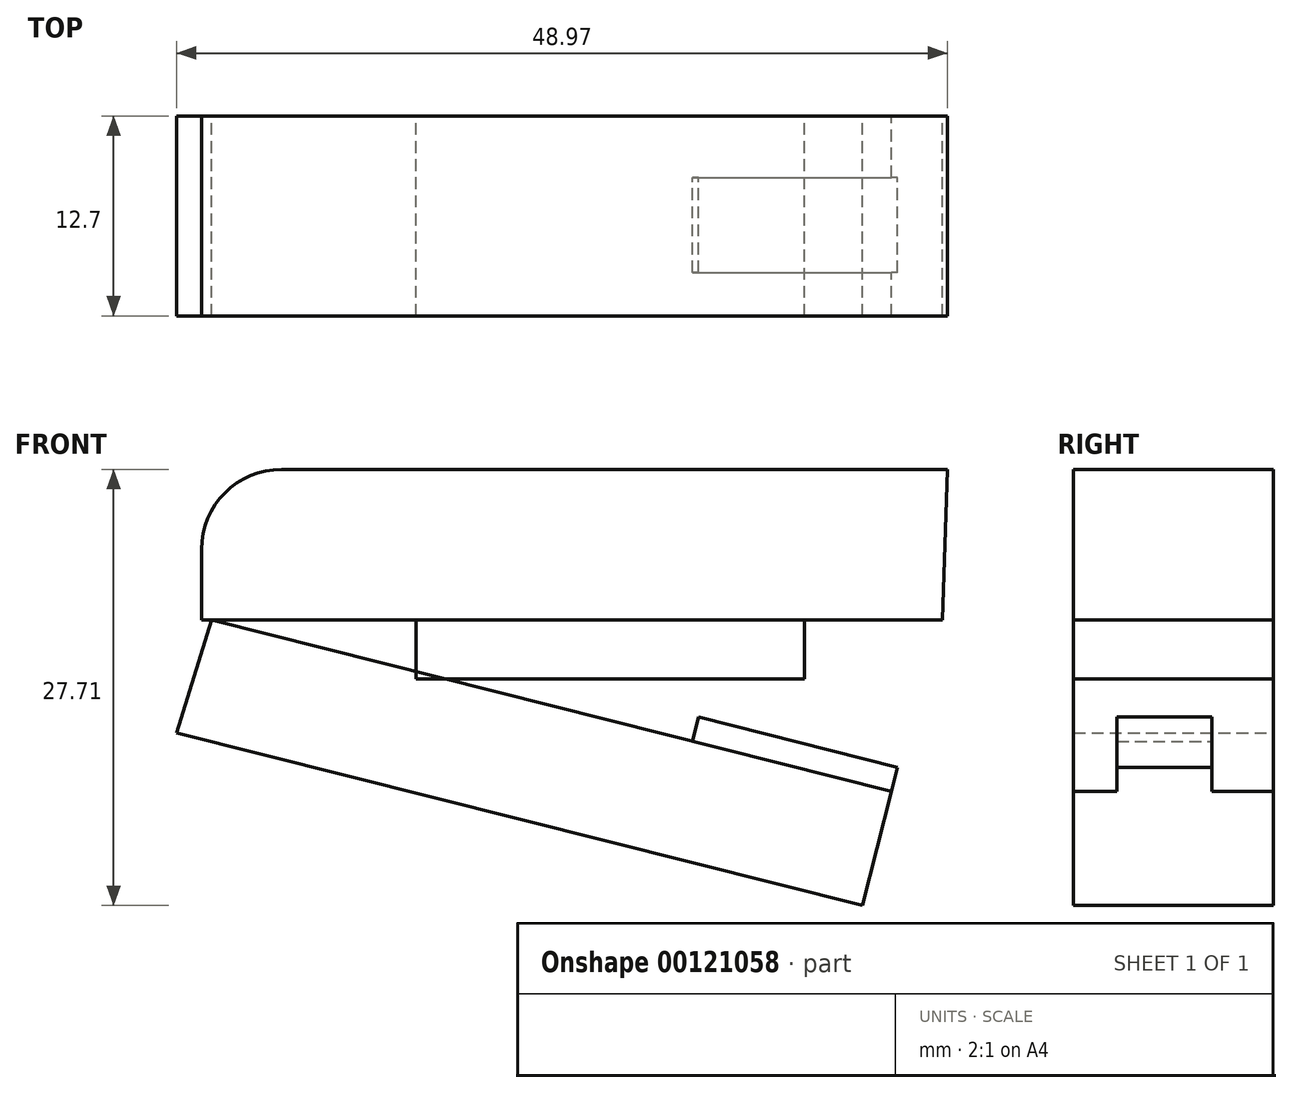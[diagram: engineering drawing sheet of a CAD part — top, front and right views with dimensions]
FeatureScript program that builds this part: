
annotation { "Feature Type Name" : "Feature", "Feature Type Description" : "" }
export const myFeature = defineFeature(function(context is Context, id is Id, definition is map)
    precondition{}
    {
        {
            var Q0;
            Q0=qCreatedBy(makeId("Front.planeOp"),FACE);
            var sketch = newSketch(context, id + "F0", { "sketchPlane" : qUnion([Q0])});
            skLineSegment(sketch, "E0", {"start": v(13.96, 0) * mm, "end": v(-33.1, 0) * mm});
            skLineSegment(sketch, "E1", {"start": v(-33.1, 0) * mm, "end": v(-33.1, 9.58) * mm});
            skLineSegment(sketch, "E2", {"start": v(-33.1, 9.58) * mm, "end": v(14.28, 9.58) * mm});
            skLineSegment(sketch, "E3", {"start": v(14.28, 9.58) * mm, "end": v(13.96, 0) * mm});
            skSolve(sketch);
        }
        {
            var Q0;
            Q0 = qSketchRegion(id + "F0", true);
            extrude(context, id + "F1", {"entities" : qUnion([Q0]), "depth" : 12.7 * mm});
        }
        {
            var Q0;
            Q0=qCreatedBy(makeId("Front.planeOp"),FACE);
            var sketch = newSketch(context, id + "F2", { "sketchPlane" : qUnion([Q0])});
            skLineSegment(sketch, "E4", {"start": v(-32.46, 0) * mm, "end": v(10.71, -10.87) * mm});
            skLineSegment(sketch, "E5", {"start": v(10.71, -10.87) * mm, "end": v(8.88, -18.13) * mm});
            skLineSegment(sketch, "E6", {"start": v(8.88, -18.13) * mm, "end": v(-34.7, -7.15) * mm});
            skLineSegment(sketch, "E7", {"start": v(-34.7, -7.15) * mm, "end": v(-32.46, 0) * mm});
            skSolve(sketch);
        }
        {
            var Q0;
            Q0 = qSketchRegion(id + "F2", true);
            extrude(context, id + "F3", {"entities" : qUnion([Q0]), "depth" : 12.7 * mm});
        }
        {
            var Q0;
            Q0=qCreatedBy(makeId("Front.planeOp"),FACE);
            var sketch = newSketch(context, id + "F4", { "sketchPlane" : qUnion([Q0])});
            skLineSegment(sketch, "E8", {"start": v(5.2, 0) * mm, "end": v(5.2, -3.73) * mm});
            skLineSegment(sketch, "E9", {"start": v(5.2, -3.73) * mm, "end": v(-19.48, -3.73) * mm});
            skLineSegment(sketch, "E10", {"start": v(-19.48, -3.73) * mm, "end": v(-19.48, 0) * mm});
            skLineSegment(sketch, "E11", {"start": v(-19.48, 0) * mm, "end": v(5.2, 0) * mm});
            skSolve(sketch);
        }
        {
            var Q0;
            Q0 = qSketchRegion(id + "F4", true);
            extrude(context, id + "F5", {"entities" : qUnion([Q0]), "depth" : 12.7 * mm});
        }
        {
            var Q0;
            Q0=makeQuery(id+"F3.opExtrude","SWEPT_FACE",FACE,{"disambiguationData":[OSD([sQuery(id+"F2.wireOp",EDGE,"E4")])]});
            var sketch = newSketch(context, id + "F6", { "sketchPlane" : qUnion([Q0])});
            skLineSegment(sketch, "E12.bottom", {"start": v(0, -9.95) * mm, "end": v(13.04, -9.95) * mm});
            skLineSegment(sketch, "E12.top", {"start": v(0, -3.92) * mm, "end": v(13.04, -3.92) * mm});
            skLineSegment(sketch, "E12.left", {"start": v(0, -9.95) * mm, "end": v(0, -3.92) * mm});
            skLineSegment(sketch, "E12.right", {"start": v(13.04, -9.95) * mm, "end": v(13.04, -3.92) * mm});
            skSolve(sketch);
        }
        {
            var Q0;
            Q0 = qSketchRegion(id + "F6", true);
            extrude(context, id + "F7", {"entities" : qUnion([Q0]), "operationType" : NewBodyOperationType.ADD, "depth" : 1.58 * mm});
        }
        {
            var Q0;
            Q0=makeQuery(id+"F1.opExtrude","SWEPT_EDGE",EDGE,{"disambiguationData":[OSD([sQuery(id+"F0.wireOp",EDGE,"E1"),sQuery(id+"F0.wireOp",EDGE,"E2")])]});
            fillet(context, id + "F8", {"entities" : qUnion([Q0]), "radius" : 5.08 * mm, "tangentPropagation" : true, "allowEdgeOverflow" : false});
        }
    });
